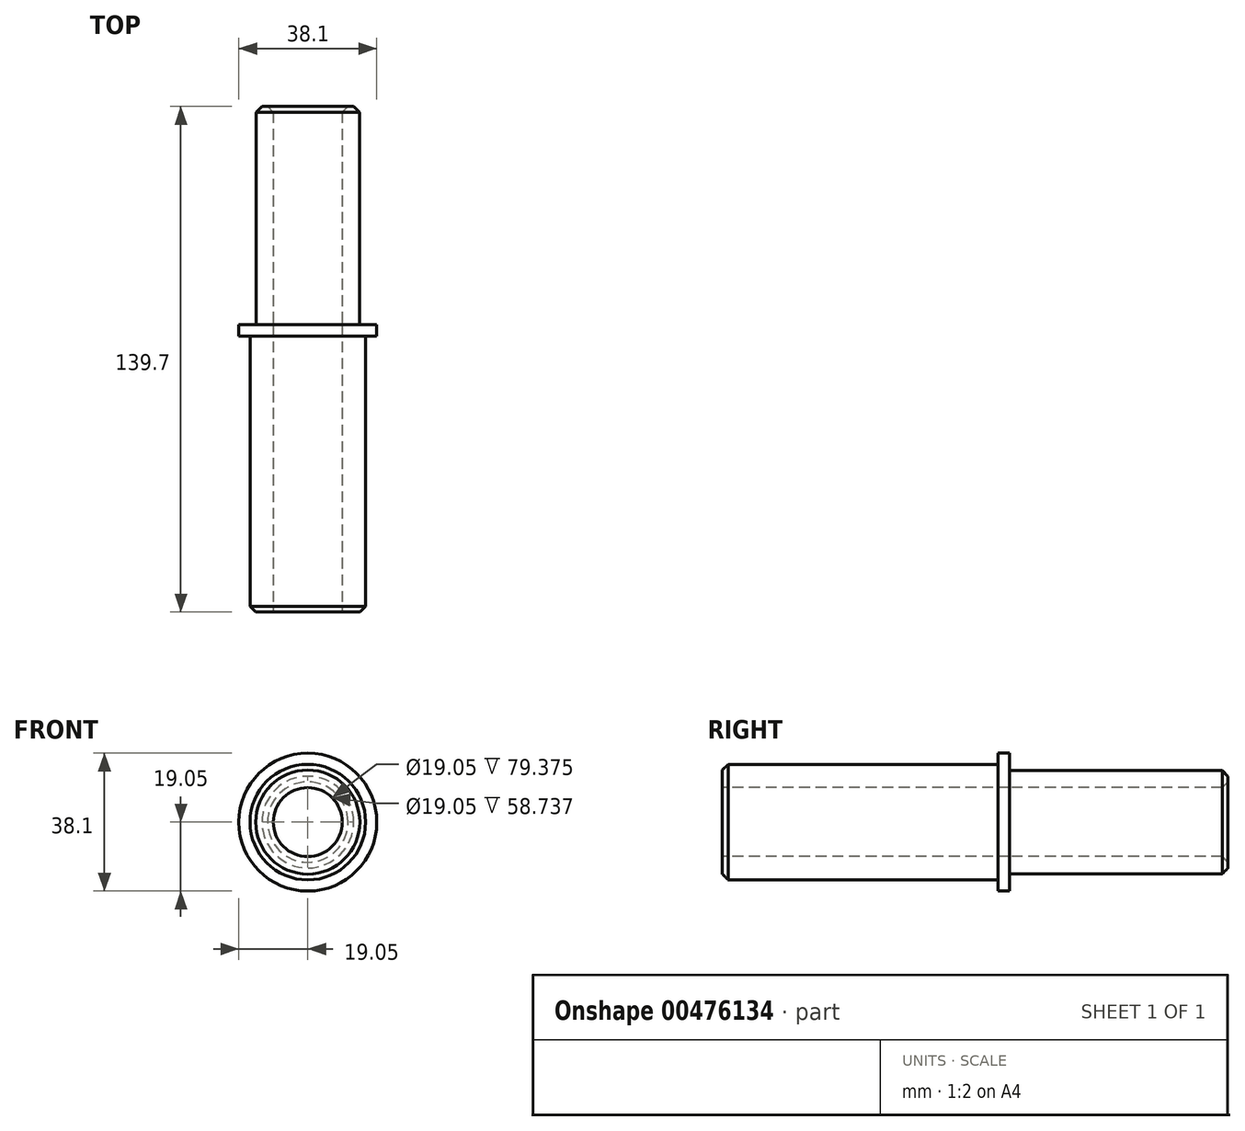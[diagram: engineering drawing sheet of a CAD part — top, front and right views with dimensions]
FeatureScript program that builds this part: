
annotation { "Feature Type Name" : "Feature", "Feature Type Description" : "" }
export const myFeature = defineFeature(function(context is Context, id is Id, definition is map)
    precondition{}
    {
        {
            var Q0;
            Q0=qCreatedBy(makeId("Front.planeOp"),FACE);
            var sketch = newSketch(context, id + "F0", { "sketchPlane" : qUnion([Q0])});
            skCircle(sketch, "E0", {"center": v(0, 0) * mm, "radius": 14.26 * mm});
            skSolve(sketch);
        }
        {
            var Q0;
            Q0=makeQuery(id+"F0.imprint","IMPRINT",FACE,{"disambiguationData":[TD([[makeQuery(id+"F0.imprint","IMPRINT",EDGE,{"derivedFrom":sQuery(id+"F0.wireOp",EDGE,"E0")}),1.0]])]});
            extrude(context, id + "F1", {"entities" : qUnion([Q0]), "depth" : 60.32 * mm});
        }
        {
            var Q0;
            Q0=makeQuery(id+"F1.opExtrude","CAP_FACE",FACE,{"disambiguationData":[OSD([sQuery(id+"F0.wireOp",EDGE,"E0")])],"isStart":false});
            var sketch = newSketch(context, id + "F2", { "sketchPlane" : qUnion([Q0])});
            skCircle(sketch, "E1", {"center": v(0, 0) * mm, "radius": 19.05 * mm});
            skSolve(sketch);
        }
        {
            var Q0;
            Q0=makeQuery(id+"F2.imprint","IMPRINT",FACE,{"disambiguationData":[TD([[makeQuery(id+"F2.imprint","IMPRINT",EDGE,{"derivedFrom":makeQuery(id+"F1.opExtrude","CAP_EDGE",EDGE,{"disambiguationData":[OSD([sQuery(id+"F0.wireOp",EDGE,"E0")])],"isStart":false})}),1.0]])]});
            var Q1;
            Q1=makeQuery(id+"F2.imprint","IMPRINT",FACE,{"disambiguationData":[TD([[makeQuery(id+"F2.imprint","IMPRINT",EDGE,{"derivedFrom":sQuery(id+"F2.wireOp",EDGE,"E1")}),1.0]])]});
            extrude(context, id + "F3", {"entities" : qUnion([Q0, Q1]), "depth" : 3.17 * mm});
        }
        {
            var Q0;
            Q0=makeQuery(id+"F3.opExtrude","CAP_FACE",FACE,{"disambiguationData":[OSD([sQuery(id+"F2.wireOp",EDGE,"E1")])],"isStart":false});
            var sketch = newSketch(context, id + "F4", { "sketchPlane" : qUnion([Q0])});
            skCircle(sketch, "E2", {"center": v(0, 0) * mm, "radius": 14.26 * mm});
            skSolve(sketch);
        }
        {
            var Q0;
            Q0=makeQuery(id+"F4.imprint","IMPRINT",FACE,{"disambiguationData":[TD([[makeQuery(id+"F4.imprint","IMPRINT",EDGE,{"derivedFrom":sQuery(id+"F4.wireOp",EDGE,"E2")}),-1.0]])]});
            var sketch = newSketch(context, id + "F5", { "sketchPlane" : qUnion([Q0])});
            skCircle(sketch, "E3", {"center": v(0, 0) * mm, "radius": 15.96 * mm});
            skSolve(sketch);
        }
        {
            var Q0;
            Q0 = qSketchRegion(id + "F5", true);
            extrude(context, id + "F6", {"entities" : qUnion([Q0]), "operationType" : NewBodyOperationType.ADD, "depth" : 76.2 * mm});
        }
        {
            var Q0;
            Q0=makeQuery(id+"F6.opExtrude","CAP_FACE",FACE,{"disambiguationData":[OSD([sQuery(id+"F5.wireOp",EDGE,"E3")])],"isStart":false});
            var sketch = newSketch(context, id + "F7", { "sketchPlane" : qUnion([Q0])});
            skCircle(sketch, "E4", {"center": v(0, 0) * mm, "radius": 9.53 * mm});
            skSolve(sketch);
        }
        {
            var Q0;
            Q0 = qSketchRegion(id + "F7", true);
            extrude(context, id + "F8", {"entities" : qUnion([Q0]), "operationType" : NewBodyOperationType.REMOVE, "endBound" : BoundingType.THROUGH_ALL, "oppositeDirection" : true, "depth" : 25.4 * mm});
        }
        {
            var Q0;
            Q0=makeQuery(id+"F1.opExtrude","CAP_EDGE",EDGE,{"disambiguationData":[OSD([sQuery(id+"F0.wireOp",EDGE,"E0")])],"isStart":true});
            var Q1;
            Q1=makeQuery(id+"F8.boolean.opBoolean","INTERSECT",EDGE,{"derivedFrom":[makeQuery(id+"F1.opExtrude","CAP_FACE",FACE,{"disambiguationData":[OSD([sQuery(id+"F0.wireOp",EDGE,"E0")])],"isStart":true}),makeQuery(id+"F8.opExtrude","SWEPT_FACE",FACE,{"disambiguationData":[OSD([sQuery(id+"F7.wireOp",EDGE,"E4")])]})]});
            var Q2;
            Q2=makeQuery(id+"F6.opExtrude","CAP_EDGE",EDGE,{"disambiguationData":[OSD([sQuery(id+"F5.wireOp",EDGE,"E3")])],"isStart":false});
            var Q3;
            Q3=makeQuery(id+"F8.boolean.opBoolean","COPY",EDGE,{"derivedFrom":makeQuery(id+"F8.opExtrude","CAP_EDGE",EDGE,{"disambiguationData":[OSD([sQuery(id+"F7.wireOp",EDGE,"E4")])],"isStart":true})});
            chamfer(context, id + "F9", {"entities" : qUnion([Q0, Q1, Q2, Q3]), "width" : 1.59 * mm, "tangentPropagation" : true});
        }
    });
